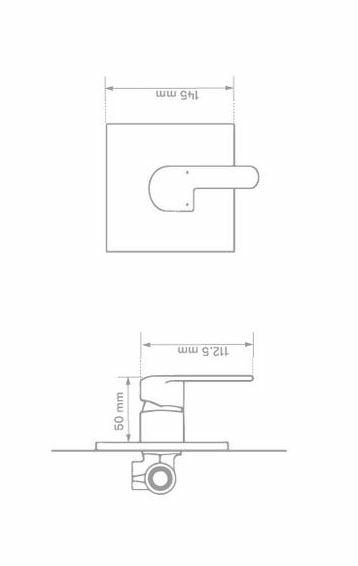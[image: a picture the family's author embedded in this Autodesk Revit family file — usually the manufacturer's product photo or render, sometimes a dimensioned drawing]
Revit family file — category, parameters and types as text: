
# Revit family: 01-1728-11 MEZCLADOR LAVAPLATOS 8 COLECCION HELIX PALA
name_source: partatom
category: Plumbing Fixtures
revit_build: Autodesk Revit 2018 (Build: 20170223_1515(x64)
units: mm (PartAtom-declared; Revit-internal decimal feet)

## family parameters
Cut with Voids When Loaded = No
Host = Face
OmniClass Number = 23.31.11.00
Part Type = Normal
Room Calculation Point = No
Round Connector Dimension = Use Diameter
Shared = No

## types (1)
- 01-1728-11
    Alto Aireador = 194 mm  [stored 0.636483 ft]
    Alto brazo = 265 mm
    Ancho brazo = 164.4 mm  [stored 0.53937 ft]
    Ancho entre manijas = 203.2 mm  [stored 0.666667 ft]
    Ancho manija = 67 mm  [stored 0.219816 ft]
    CW Connection = Yes
    Default Elevation = 0 mm  [stored 0 ft]
    Description = Bimando
    HW Connection = Yes
    Link Ficha Tecnica = http://infotecnica.gricol.com
    Manufacturer = Gricol
    Model = 01-1728-11
    Plástico - ABS Cromado = Plastico ABS Cromado
    Product Name = MEZCLADOR LAVAPLATOS 8 COLECCION HELIX PALA
    Type Image = <None>
    URL = https://www.gricol.com
    Vent Connection = No
    Waste Connection = No

note: [stored X ft] marks values corroborated as IEEE doubles in the binary element streams (Revit-internal decimal feet)

## geometry (parser evidence)
native form markers: Blend x2, Sweep x2
no freeform markers — native parametric forms only
